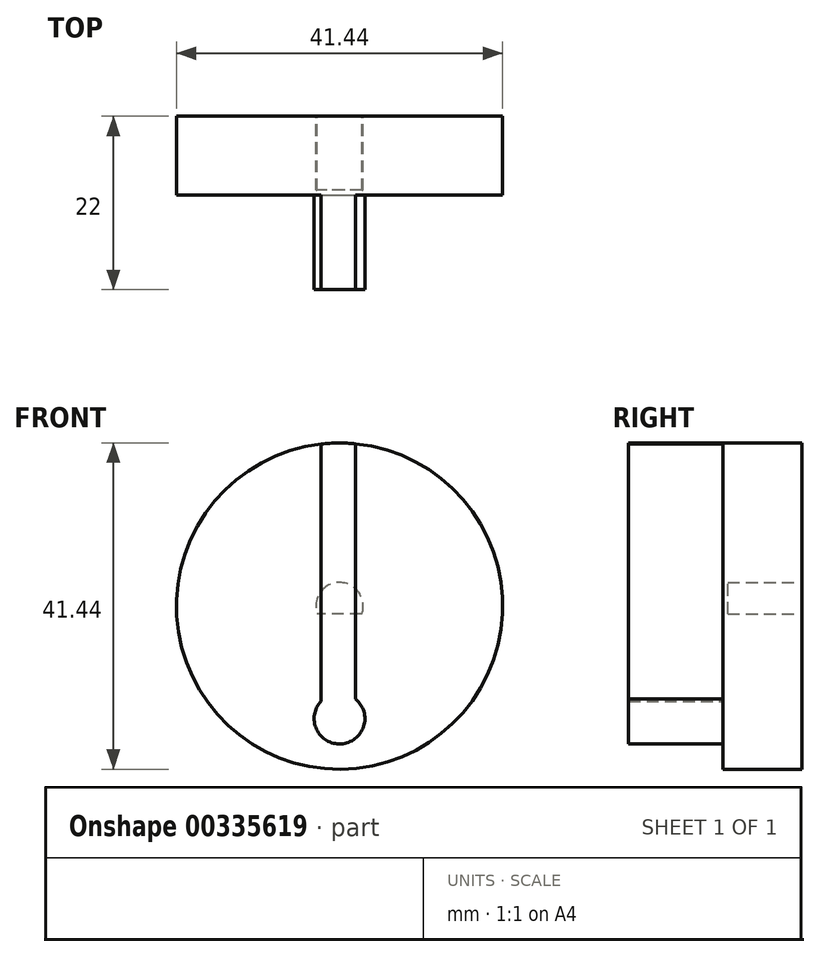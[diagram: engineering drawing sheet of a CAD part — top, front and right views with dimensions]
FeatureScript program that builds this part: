
annotation { "Feature Type Name" : "Feature", "Feature Type Description" : "" }
export const myFeature = defineFeature(function(context is Context, id is Id, definition is map)
    precondition{}
    {
        {
            var Q0;
            Q0=qCreatedBy(makeId("Front.planeOp"),FACE);
            var sketch = newSketch(context, id + "F0", { "sketchPlane" : qUnion([Q0])});
            skCircle(sketch, "E0", {"center": v(0, 0) * mm, "radius": 20.72 * mm});
            skSolve(sketch);
        }
        {
            var Q0;
            Q0 = qSketchRegion(id + "F0", true);
            extrude(context, id + "F1", {"entities" : qUnion([Q0]), "depth" : 10 * mm});
        }
        {
            var Q0;
            Q0=makeQuery(id+"F1.opExtrude","CAP_FACE",FACE,{"disambiguationData":[OSD([sQuery(id+"F0.wireOp",EDGE,"E0")])],"isStart":true});
            var sketch = newSketch(context, id + "F2", { "sketchPlane" : qUnion([Q0])});
            skCircle(sketch, "E1", {"center": v(0, 0) * mm, "radius": 18.32 * mm});
            skSolve(sketch);
        }
        {
            var Q0;
            Q0 = qSketchRegion(id + "F2", true);
            extrude(context, id + "F3", {"entities" : qUnion([Q0]), "operationType" : NewBodyOperationType.ADD, "oppositeDirection" : true, "depth" : 8 * mm});
        }
        {
            var Q0;
            Q0=makeQuery(id+"F1.opExtrude","CAP_FACE",FACE,{"disambiguationData":[OSD([sQuery(id+"F0.wireOp",EDGE,"E0")])],"isStart":false});
            var sketch = newSketch(context, id + "F4", { "sketchPlane" : qUnion([Q0])});
            skCircle(sketch, "E2", {"center": v(0, -14.3) * mm, "radius": 3.22 * mm});
            skLineSegment(sketch, "E3", {"start": v(2.05, -11.81) * mm, "end": v(2.05, 20.62) * mm});
            skLineSegment(sketch, "E4", {"start": v(-2.34, -12.08) * mm, "end": v(-2.34, 20.59) * mm});
            skSolve(sketch);
        }
        {
            var Q0;
            Q0 = qSketchRegion(id + "F4", true);
            var Q1;
            {var subQ0=sQuery(id+"F4.wireOp",EDGE,"E3");Q1=makeQuery(id+"F4.imprint","IMPRINT",FACE,{"disambiguationData":[TD([[makeQuery(id+"F4.imprint","IMPRINT",EDGE,{"derivedFrom":subQ0}),1.0]])]});}
            extrude(context, id + "F5", {"entities" : qUnion([Q0, Q1]), "operationType" : NewBodyOperationType.ADD, "depth" : 12 * mm});
        }
        {
            var Q0;
            Q0=qCreatedBy(makeId("Front.planeOp"),FACE);
            var sketch = newSketch(context, id + "F6", { "sketchPlane" : qUnion([Q0])});
            skCircle(sketch, "E5", {"center": v(0, 0) * mm, "radius": 3 * mm});
            skLineSegment(sketch, "E6", {"start": v(2.83, -1) * mm, "end": v(-2.83, -1) * mm});
            skSolve(sketch);
        }
        {
            var Q0;
            {var subQ0=sQuery(id+"F6.wireOp",EDGE,"E6");Q0=makeQuery(id+"F6.imprint","IMPRINT",FACE,{"disambiguationData":[TD([[makeQuery(id+"F6.imprint","IMPRINT",EDGE,{"derivedFrom":subQ0}),-1.0]])]});}
            extrude(context, id + "F7", {"entities" : qUnion([Q0]), "operationType" : NewBodyOperationType.REMOVE, "depth" : 9.4 * mm});
        }
    });
